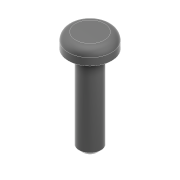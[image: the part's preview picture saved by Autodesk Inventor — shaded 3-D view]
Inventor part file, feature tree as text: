
AUTODESK INVENTOR PART (.ipt)
format: ipt  version: 2022 (Build 260153000, 153)  size: 108,032 bytes
history: native  units: mm
features: extrude x2, sketch x2, chamfer x1, fillet x1
ambient origin geometry x8: Origin, YZ Plane, XZ Plane, XY Plane, X Axis, Y Axis, Z Axis, Center Point
bodies: Solid1 (feature_tree)
feature tree (6):
  extrude  "Extrusion1"  Depth=2.0mm TaperAngle=0.0deg
  extrude  "Extrusion2"  Depth=12.0mm TaperAngle=0.0deg
  chamfer  "Chamfer1"  Distance=2.0mm Angle=45.0deg
  fillet  "Fillet1"  Radius=1.0mm
  sketch  "Sketch1"  dims[d0=6.0mm d1=2.0mm d2=0.0mm]
  sketch  "Sketch2"  dims[d3=3.0mm d4=12.0mm d5=0.0mm d6=0.5mm d7=2.0mm d8=45.0deg d9=1.0mm]
